# Revit family: Центральный пульт управления ESVM-A64S
name_source: partatom
category: Mechanical Equipment
revit_build: Autodesk Revit 2016 (Build: 20150506_1715(x64)
units: mm (PartAtom-declared; Revit-internal decimal feet)

## family parameters
Cut with Voids When Loaded = No
Host = Face
Part Type = Normal
Room Calculation Point = No
Round Connector Dimension = Use Diameter
Shared = No

## types (1)
- ESVM-A64S
    Default Elevation = 1219.2 mm  [stored 4 ft]
    Артикул = 1022723
    Вес = 0.40 kg
    Высота = 120 mm  [stored 0.393701 ft]
    Глубина = 20 mm  [stored 0.0656168 ft]
    Максимальное кол-во подключаемых внутренних блоков, шт = 1024
    Модель = ESVM-A64S
    Наименование = Центральный пульт управления
    Производитель = Electrolux
    Таблица модель = Модель
    Таблица наименование = Наименование
    Таблица параметров = Таблица параметров
    Таблица частота сети = Частота сети
    Таблица электропитание = Электропитание
    Фаза = 1
    Частота сети = 50 Hz
    Ширина = 120 mm  [stored 0.393701 ft]
    Эл. питание(коннектор) = 220 V
    Электропитание, (В) = 220

note: [stored X ft] marks values corroborated as IEEE doubles in the binary element streams (Revit-internal decimal feet)
